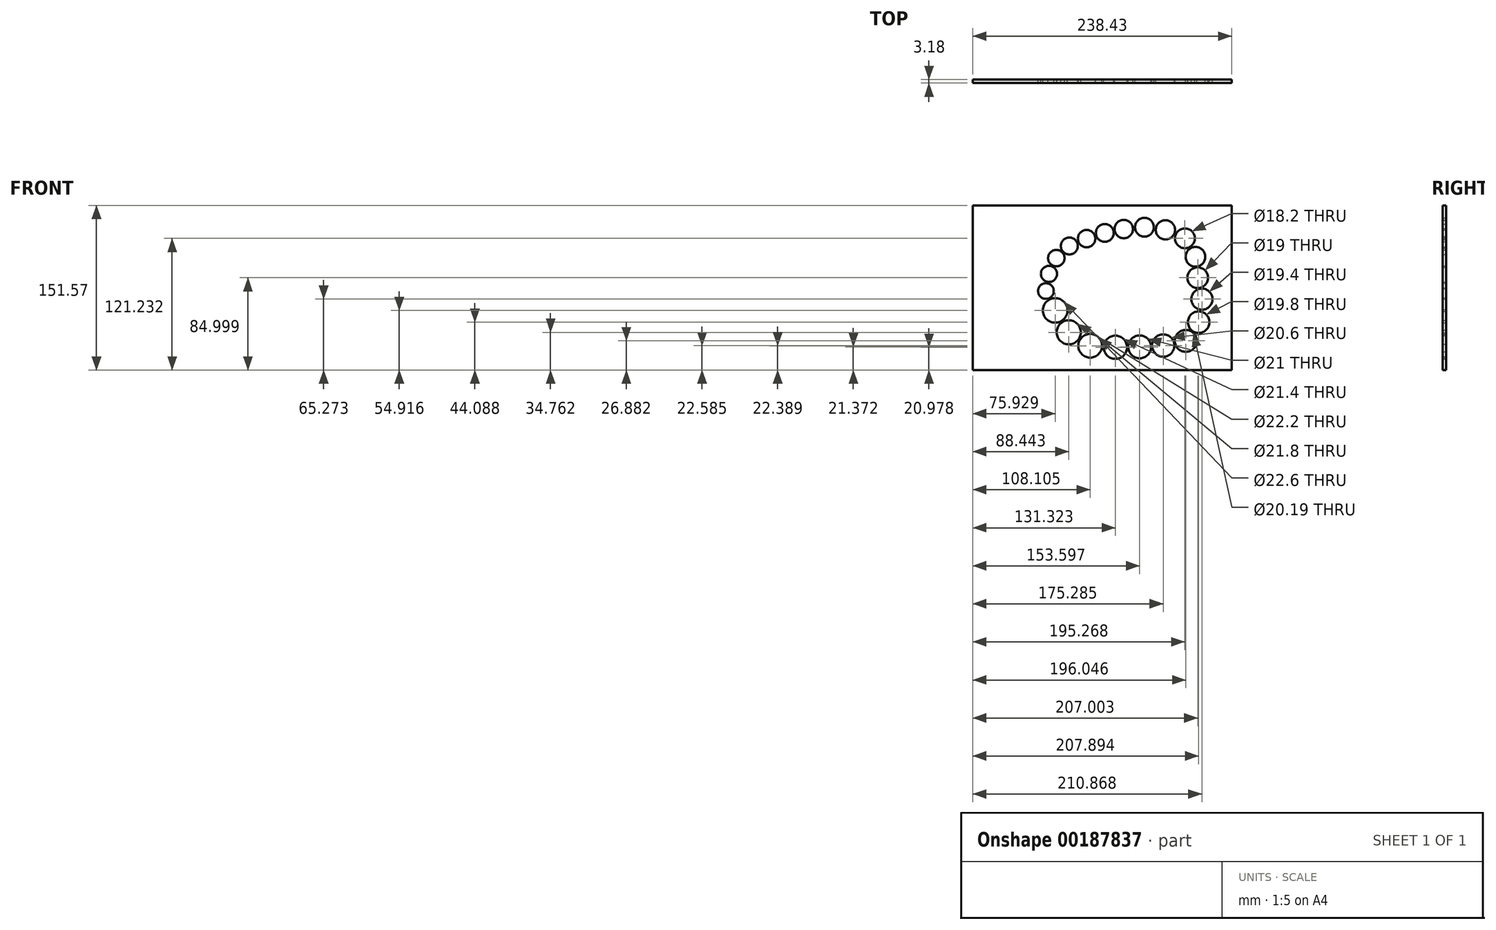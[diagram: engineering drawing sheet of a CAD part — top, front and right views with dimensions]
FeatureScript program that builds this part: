
annotation { "Feature Type Name" : "Feature", "Feature Type Description" : "" }
export const myFeature = defineFeature(function(context is Context, id is Id, definition is map)
    precondition{}
    {
        {
            var Q0;
            Q0=qCreatedBy(makeId("Front.planeOp"),FACE);
            var sketch = newSketch(context, id + "F0", { "sketchPlane" : qUnion([Q0])});
            skCircle(sketch, "E0", {"center": v(-65.7, -2.87) * mm, "radius": 7.22 * mm});
            skCircle(sketch, "E1", {"center": v(-62.9, 12.85) * mm, "radius": 7.4 * mm});
            skCircle(sketch, "E2", {"center": v(-56.14, 27.4) * mm, "radius": 7.6 * mm});
            skCircle(sketch, "E3", {"center": v(-44.12, 38.55) * mm, "radius": 7.8 * mm});
            skCircle(sketch, "E4", {"center": v(-28.32, 45.3) * mm, "radius": 8 * mm});
            skCircle(sketch, "E5", {"center": v(-11.59, 50.57) * mm, "radius": 8.22 * mm});
            skCircle(sketch, "E6", {"center": v(5.9, 54.14) * mm, "radius": 8.45 * mm});
            skCircle(sketch, "E7", {"center": v(24.9, 55.78) * mm, "radius": 8.65 * mm});
            skCircle(sketch, "E8", {"center": v(44.18, 53.37) * mm, "radius": 8.85 * mm});
            skCircle(sketch, "E9", {"center": v(62.14, 45.6) * mm, "radius": 9.1 * mm});
            skSolve(sketch);
        }
        {
            var Q0;
            Q0=qCreatedBy(makeId("Front.planeOp"),FACE);
            var sketch = newSketch(context, id + "F1", { "sketchPlane" : qUnion([Q0])});
            skCircle(sketch, "E10", {"center": v(71.8, 28.63) * mm, "radius": 9.05 * mm});
            skCircle(sketch, "E11", {"center": v(73.87, 9.36) * mm, "radius": 9.5 * mm});
            skCircle(sketch, "E12", {"center": v(77.74, -10.37) * mm, "radius": 9.7 * mm});
            skCircle(sketch, "E13", {"center": v(74.76, -31.55) * mm, "radius": 9.9 * mm});
            skCircle(sketch, "E14", {"center": v(42.15, -53.05) * mm, "radius": 10.3 * mm});
            skCircle(sketch, "E15", {"center": v(20.47, -54.27) * mm, "radius": 10.5 * mm});
            skCircle(sketch, "E16", {"center": v(-1.8, -54.66) * mm, "radius": 10.7 * mm});
            skCircle(sketch, "E17", {"center": v(-25.02, -53.25) * mm, "radius": 10.9 * mm});
            skCircle(sketch, "E18", {"center": v(-44.69, -40.88) * mm, "radius": 11.1 * mm});
            skCircle(sketch, "E19", {"center": v(-57.2, -20.72) * mm, "radius": 11.3 * mm});
            skCircle(sketch, "E20", {"center": v(62.92, -48.76) * mm, "radius": 10.1 * mm});
            skSolve(sketch);
        }
        {
            var Q0;
            Q0=qCreatedBy(makeId("Front.planeOp"),FACE);
            var sketch = newSketch(context, id + "F2", { "sketchPlane" : qUnion([Q0])});
            skLineSegment(sketch, "E21.bottom", {"start": v(-133.13, 75.93) * mm, "end": v(105.3, 75.93) * mm});
            skLineSegment(sketch, "E21.top", {"start": v(-133.13, -75.64) * mm, "end": v(105.3, -75.64) * mm});
            skLineSegment(sketch, "E21.left", {"start": v(-133.13, 75.93) * mm, "end": v(-133.13, -75.64) * mm});
            skLineSegment(sketch, "E21.right", {"start": v(105.3, 75.93) * mm, "end": v(105.3, -75.64) * mm});
            skSolve(sketch);
        }
        {
            var Q0;
            Q0=makeQuery(id+"F2.imprint","IMPRINT",FACE,{"disambiguationData":[TD([[makeQuery(id+"F2.imprint","IMPRINT",EDGE,{"derivedFrom":sQuery(id+"F2.wireOp",EDGE,"E21.bottom")}),-1.0]])]});
            extrude(context, id + "F3", {"entities" : qUnion([Q0]), "depth" : 3.17 * mm});
        }
        {
            var Q0;
            Q0 = qSketchRegion(id + "F1", true);
            var Q1;
            Q1 = qSketchRegion(id + "F0", true);
            extrude(context, id + "F4", {"entities" : qUnion([Q0, Q1]), "operationType" : NewBodyOperationType.REMOVE, "depth" : 25.4 * mm});
        }
    });
